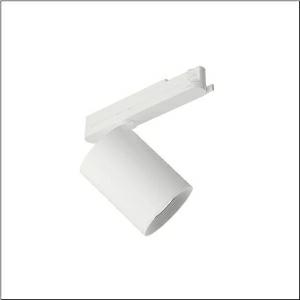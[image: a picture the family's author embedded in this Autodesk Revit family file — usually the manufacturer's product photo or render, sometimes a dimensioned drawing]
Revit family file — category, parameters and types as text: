
# Revit family: spot_11_51sd14mbd5a
name_source: partatom
category: Lighting Fixtures
units: mm (PartAtom-declared; Revit-internal decimal feet)

## family parameters
Cut with Voids When Loaded = No
Host = Face
Light Source = No
Part Type = Normal
Room Calculation Point = No
Round Connector Dimension = Use Diameter
Shared = No

## types (1)
- --- (1 x LED, 7420 lm, 50.3 W, 4000K)
    Apparent Load = 50 VA
    CIE Flux Codes = 95 98 100 100 100
    Color Rendering = 90
    Color Temperature = 4000K
    Default Elevation = 1800 mm
    Description = Spot 11, directional spotlight, light control with lens, of PMMA, LED rated luminous flux: 5.670lm, light colour: 940, control gear: ECG Multilumen, with 3-phase adapter, mains connection: 220..240V, AC, 50/60Hz, of aluminium, traffic white (RAL 9016), length: 213mm, diameter: 105mm, protection rating (complete): IP20, insulation class (complete): insulation class I (protective earthing), certification: CE, impact resistance: IK02, permissible ambient temperature for indoor applications: -20..+40°C, packaging unit: 1 piece
    Height = 175 mm
    Lamp = 1 x LED
    Lamp Light Flux = 7420 lm
    Lamp Power = 50.3 W
    Lamp count = 1
    Length = 105 mm
    Luminous efficacy = 148 lm/W
    Manufacturer = Siteco
    ModVariant = No
    Model = 51SD14MBD5A
    Mounting Place = Ceiling
    Mounting Type = Pendant
    Number of Poles = 1
    OnlyDefault = Yes
    Power Factor = 1
    Product Name = Spot 11
    Product group = directional spotlight
    ProductGroupID = 905
    Protection Class = Protection class I
    Protection Degree = IP 20
    RLX_Detail_Level = 1
    RLX_Emergency_Light_Flux = 0 lm
    RLX_Emergency_Type = 0
    RLX_Emergency_Type_DB = No
    RlxData = <blob elided: 17681 chars, md5=73293ad2>
    Socket = socket
    Standby Power = 0 W
    System Light Flux = 7420 lm
    System Power = 50 W
    Type Comments = factory setting: luminous flux: 100 % | (ON | ON | ON | ON) | 1050 mA
    Type Image = l_1006697.jpg
    URL = http://relux.com
    VarID = @adj_146937
    Voltage = 0 V
    Weight = 0.00 kg
    Width = 0 mm  [stored 0 ft]

note: [stored X ft] marks values corroborated as IEEE doubles in the binary element streams (Revit-internal decimal feet)

## geometry (parser evidence)
native form markers: Blend x4, Sweep x10
no freeform markers — native parametric forms only
